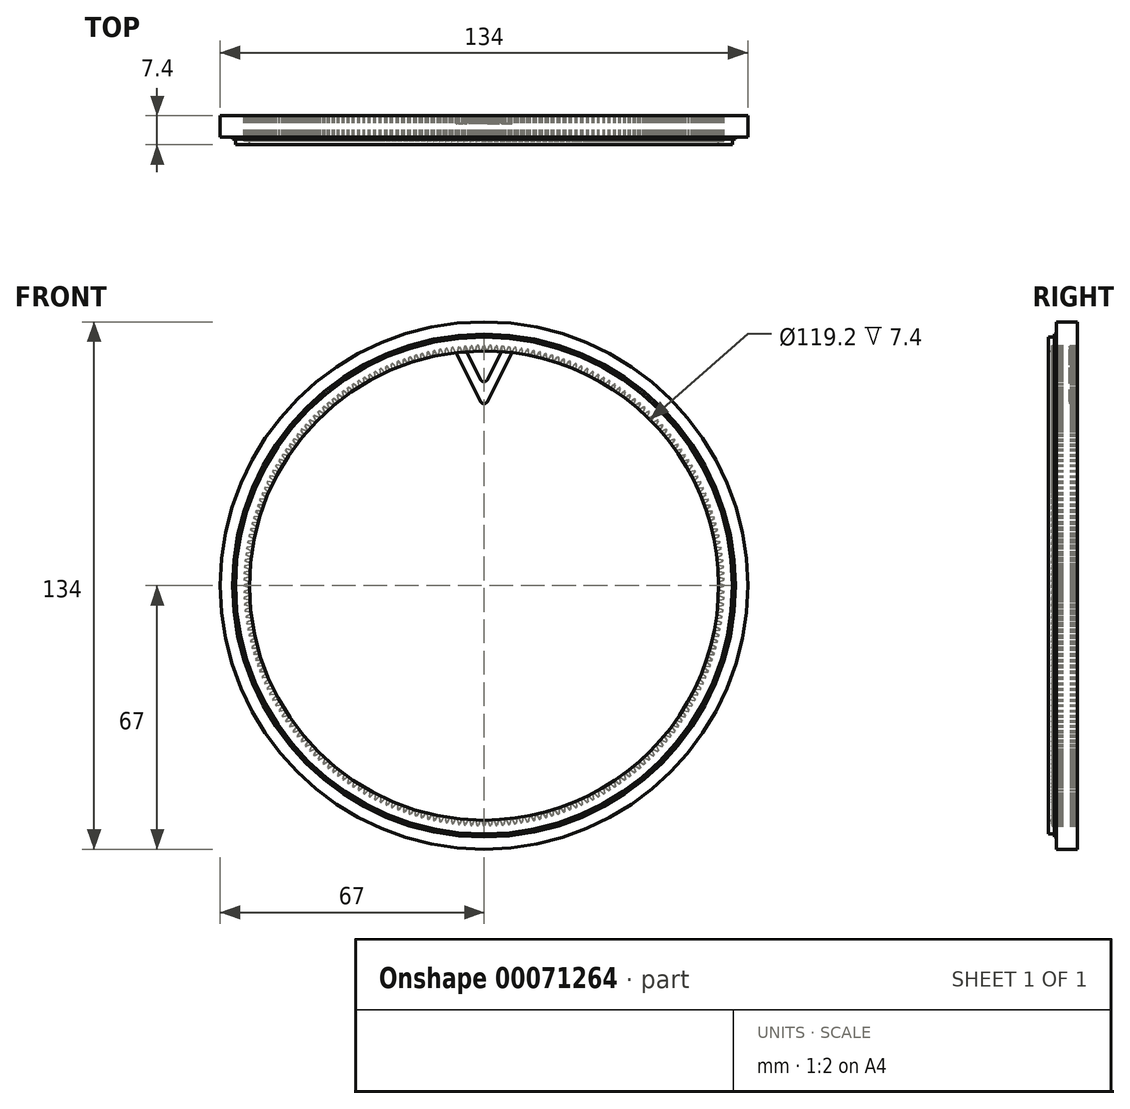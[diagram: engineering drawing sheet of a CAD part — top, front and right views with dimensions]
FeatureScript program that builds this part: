
annotation { "Feature Type Name" : "Feature", "Feature Type Description" : "" }
export const myFeature = defineFeature(function(context is Context, id is Id, definition is map)
    precondition{}
    {
        {
            var Q0;
            Q0=qCreatedBy(makeId("Front.planeOp"),FACE);
            var sketch = newSketch(context, id + "F0", { "sketchPlane" : qUnion([Q0])});
            skCircle(sketch, "E0", {"center": v(0, 0) * mm, "radius": 67 * mm});
            skCircle(sketch, "E1", {"center": v(0, 0) * mm, "radius": 59.6 * mm});
            skSolve(sketch);
        }
        {
            var Q0;
            Q0=makeQuery(id+"F0.imprint","IMPRINT",FACE,{"disambiguationData":[TD([[makeQuery(id+"F0.imprint","IMPRINT",EDGE,{"derivedFrom":sQuery(id+"F0.wireOp",EDGE,"E0")}),1.0]])]});
            extrude(context, id + "F1", {"entities" : qUnion([Q0]), "endBound" : BoundingType.SYMMETRIC, "depth" : 7.4 * mm});
        }
        {
            var Q0;
            Q0=makeQuery(id+"F1.opExtrude","CAP_FACE",FACE,{"disambiguationData":[OSD([sQuery(id+"F0.wireOp",EDGE,"E0"),sQuery(id+"F0.wireOp",EDGE,"E1")])],"isStart":false});
            var sketch = newSketch(context, id + "F2", { "sketchPlane" : qUnion([Q0])});
            skCircle(sketch, "E2", {"center": v(0, 0) * mm, "radius": 63.88 * mm});
            skCircle(sketch, "E3", {"center": v(0, 0) * mm, "radius": 63.12 * mm});
            skSolve(sketch);
        }
        {
            var Q0;
            Q0=makeQuery(id+"F2.imprint","IMPRINT",FACE,{"disambiguationData":[TD([[makeQuery(id+"F2.imprint","IMPRINT",EDGE,{"derivedFrom":sQuery(id+"F2.wireOp",EDGE,"E2")}),1.0]])]});
            extrude(context, id + "F3", {"entities" : qUnion([Q0]), "operationType" : NewBodyOperationType.REMOVE, "oppositeDirection" : true, "depth" : 1.5 * mm});
        }
        {
            var Q0;
            {var subQ0=sQuery(id+"F0.wireOp",EDGE,"E0");Q0=makeQuery(id+"F3.boolean.opBoolean","SPLIT",FACE,{"disambiguationData":[TD([makeQuery(id+"F1.opExtrude","SWEPT_FACE",FACE,{"disambiguationData":[OSD([subQ0])]})])],"derivedFrom":makeQuery(id+"F1.opExtrude","CAP_FACE",FACE,{"disambiguationData":[OSD([subQ0,sQuery(id+"F0.wireOp",EDGE,"E1")])],"isStart":false})});}
            extrude(context, id + "F4", {"entities" : qUnion([Q0]), "operationType" : NewBodyOperationType.REMOVE, "oppositeDirection" : true, "depth" : 2 * mm});
        }
        {
            var Q0;
            Q0=makeQuery(id+"F1.opExtrude","CAP_FACE",FACE,{"disambiguationData":[OSD([sQuery(id+"F0.wireOp",EDGE,"E0"),sQuery(id+"F0.wireOp",EDGE,"E1")])],"isStart":true});
            var sketch = newSketch(context, id + "F5", { "sketchPlane" : qUnion([Q0])});
            skCircle(sketch, "E4", {"center": v(0, 0) * mm, "radius": 61 * mm, "construction": true});
            skLineSegment(sketch, "E5", {"start": v(0, 0) * mm, "end": v(61, 0) * mm, "construction": true});
            skLineSegment(sketch, "E6", {"start": v(61, 0.15) * mm, "end": v(61, -0.15) * mm});
            skPoint(sketch, "E7", {"position": v(59.4, 0) * mm});
            skLineSegment(sketch, "E8", {"start": v(59.4, 0.67) * mm, "end": v(59.4, -0.68) * mm});
            skLineSegment(sketch, "E9", {"start": v(59.4, 0.68) * mm, "end": v(61, 0.15) * mm});
            skLineSegment(sketch, "E10", {"start": v(59.4, -0.68) * mm, "end": v(61, -0.15) * mm});
            skSolve(sketch);
        }
        {
            var Q0;
            {var subQ0=sQuery(id+"F5.wireOp",EDGE,"E6");Q0=makeQuery(id+"F5.imprint","IMPRINT",FACE,{"disambiguationData":[TD([[makeQuery(id+"F5.imprint","IMPRINT",EDGE,{"derivedFrom":subQ0}),-1.0]])]});}
            extrude(context, id + "F6", {"entities" : qUnion([Q0]), "operationType" : NewBodyOperationType.REMOVE, "oppositeDirection" : true, "depth" : 6.5 * mm});
        }
        {
            var Q0;
            Q0=makeQuery(id+"F6.boolean.opBoolean","COPY",FACE,{"derivedFrom":makeQuery(id+"F6.opExtrude","CAP_FACE",FACE,{"disambiguationData":[OSD([sQuery(id+"F0.wireOp",EDGE,"E1"),sQuery(id+"F5.wireOp",EDGE,"E6"),sQuery(id+"F5.wireOp",EDGE,"E9"),sQuery(id+"F5.wireOp",EDGE,"E10")])],"isStart":false})});
            var Q1;
            Q1=makeQuery(id+"F6.boolean.opBoolean","COPY",FACE,{"derivedFrom":makeQuery(id+"F6.opExtrude","SWEPT_FACE",FACE,{"disambiguationData":[OSD([sQuery(id+"F5.wireOp",EDGE,"E9")])]})});
            var Q2;
            Q2=makeQuery(id+"F6.boolean.opBoolean","COPY",FACE,{"derivedFrom":makeQuery(id+"F6.opExtrude","SWEPT_FACE",FACE,{"disambiguationData":[OSD([sQuery(id+"F5.wireOp",EDGE,"E6")])]})});
            var Q3;
            Q3=makeQuery(id+"F6.boolean.opBoolean","COPY",FACE,{"derivedFrom":makeQuery(id+"F6.opExtrude","SWEPT_FACE",FACE,{"disambiguationData":[OSD([sQuery(id+"F5.wireOp",EDGE,"E10")])]})});
            var Q4;
            Q4=makeQuery(id+"F1.opExtrude","SWEPT_FACE",FACE,{"disambiguationData":[OSD([sQuery(id+"F0.wireOp",EDGE,"E1")])]});
            circularPattern(context, id + "F7", {"faces" : qUnion([Q0, Q1, Q2, Q3]), "axis" : qUnion([Q4]), "angle" : 360 * degree, "instanceCount" : 240, "equalSpace" : true, "patternType" : PatternType.FACE});
        }
        {
            var Q0;
            Q0=makeQuery(id+"F1.opExtrude","CAP_FACE",FACE,{"disambiguationData":[OSD([sQuery(id+"F0.wireOp",EDGE,"E0"),sQuery(id+"F0.wireOp",EDGE,"E1")])],"isStart":true});
            var sketch = newSketch(context, id + "F8", { "sketchPlane" : qUnion([Q0])});
            skCircle(sketch, "E11.0", {"center": v(0, 0) * mm, "radius": 63.12 * mm, "construction": true});
            skLineSegment(sketch, "E12", {"start": v(0, 0) * mm, "end": v(0, 45) * mm, "construction": true});
            skLineSegment(sketch, "E13", {"start": v(0, 0) * mm, "end": v(8.79, 62.51) * mm, "construction": true});
            skLineSegment(sketch, "E14", {"start": v(0, 45) * mm, "end": v(8.79, 62.51) * mm});
            skLineSegment(sketch, "E15", {"start": v(8.79, 62.51) * mm, "end": v(0, 62.51) * mm});
            skLineSegment(sketch, "E16.MirrorCS", {"start": v(0, 45) * mm, "end": v(-8.79, 62.51) * mm});
            skLineSegment(sketch, "E17.MirrorCS", {"start": v(-8.79, 62.51) * mm, "end": v(0, 62.51) * mm});
            skLineSegment(sketch, "E18.0", {"start": v(4.73, 60.01) * mm, "end": v(0, 60.01) * mm});
            skLineSegment(sketch, "E18.1", {"start": v(0, 50.57) * mm, "end": v(4.73, 60.01) * mm});
            skLineSegment(sketch, "E18.2", {"start": v(0, 50.57) * mm, "end": v(-4.73, 60.01) * mm});
            skLineSegment(sketch, "E18.3", {"start": v(-4.73, 60.01) * mm, "end": v(0, 60.01) * mm});
            skSolve(sketch);
        }
        {
            var Q0;
            {var subQ19=sQuery(id+"F8.wireOp",EDGE,"E15");Q0=makeQuery(id+"F8.imprint","IMPRINT",FACE,{"disambiguationData":[TD([[makeQuery(id+"F8.imprint","IMPRINT",EDGE,{"derivedFrom":subQ19}),1.0]])]});}
            var Q1;
            {var subQ17=sQuery(id+"F8.wireOp",EDGE,"E18.1");Q1=makeQuery(id+"F8.imprint","IMPRINT",FACE,{"disambiguationData":[TD([[makeQuery(id+"F8.imprint","IMPRINT",EDGE,{"derivedFrom":subQ17}),-1.0]])]});}
            extrude(context, id + "F9", {"entities" : qUnion([Q0, Q1]), "operationType" : NewBodyOperationType.ADD, "oppositeDirection" : true, "depth" : 2 * mm});
        }
        {
            var Q0;
            Q0=makeQuery(id+"F9.opExtrude","SWEPT_EDGE",EDGE,{"disambiguationData":[OSD([sQuery(id+"F8.wireOp",EDGE,"E14"),sQuery(id+"F8.wireOp",EDGE,"E16.MirrorCS")])]});
            var Q1;
            Q1=makeQuery(id+"F9.opExtrude","SWEPT_EDGE",EDGE,{"disambiguationData":[OSD([sQuery(id+"F8.wireOp",EDGE,"E18.1"),sQuery(id+"F8.wireOp",EDGE,"E18.2")])]});
            fillet(context, id + "F10", {"entities" : qUnion([Q0, Q1]), "radius" : 1 * mm, "tangentPropagation" : true, "allowEdgeOverflow" : false});
        }
    });
